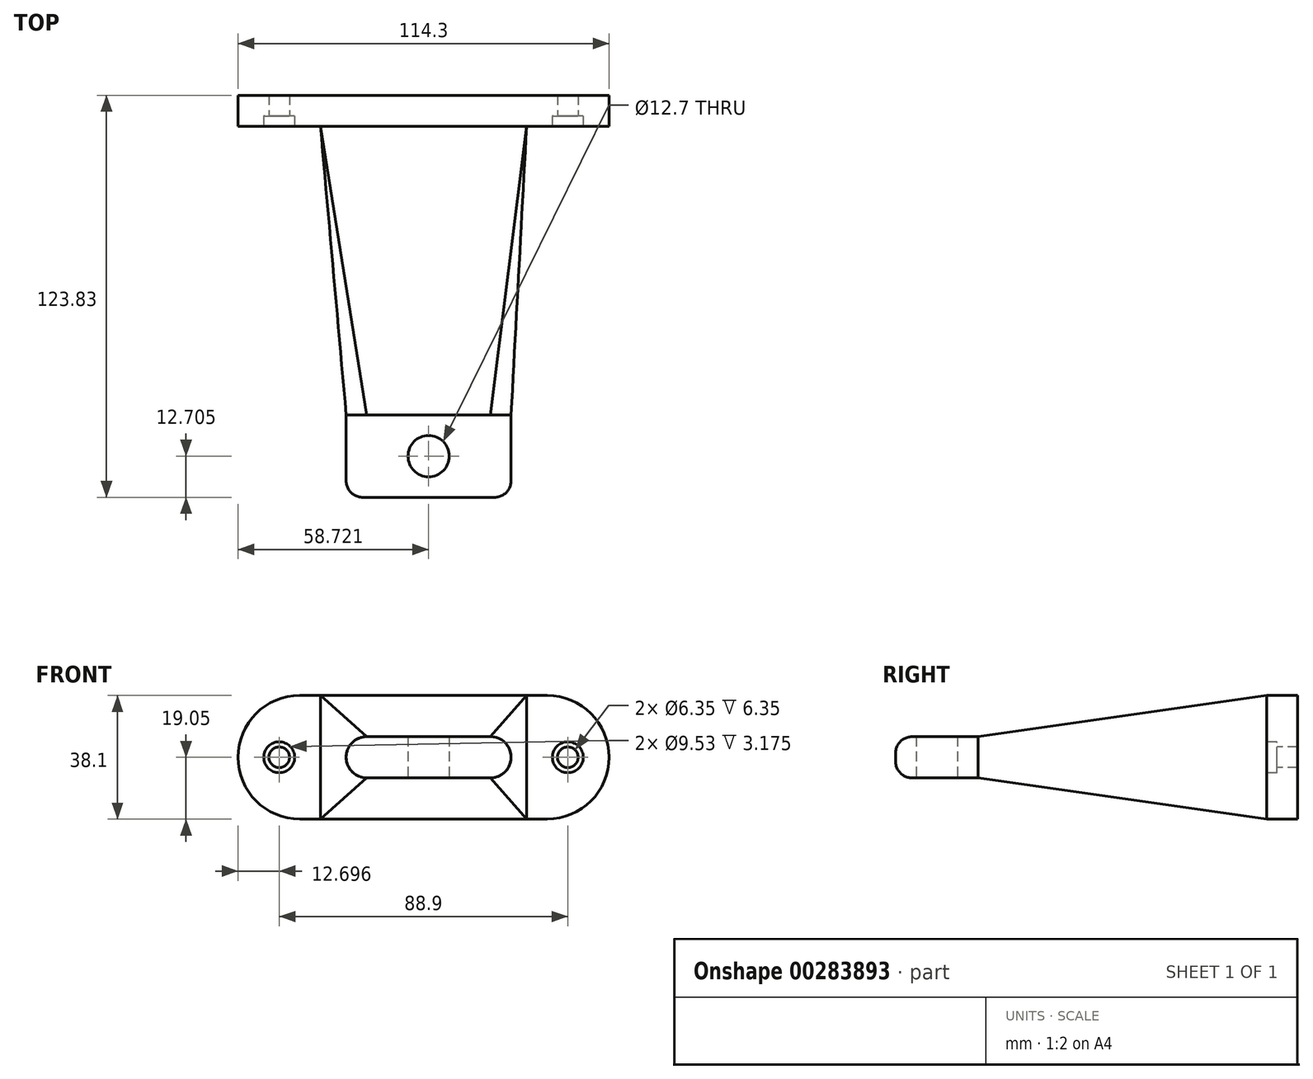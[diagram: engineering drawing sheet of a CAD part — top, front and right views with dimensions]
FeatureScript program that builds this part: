
annotation { "Feature Type Name" : "Feature", "Feature Type Description" : "" }
export const myFeature = defineFeature(function(context is Context, id is Id, definition is map)
    precondition{}
    {
        {
            var Q0;
            Q0=qCreatedBy(makeId("Front.planeOp"),FACE);
            var sketch = newSketch(context, id + "F0", { "sketchPlane" : qUnion([Q0])});
            skArc(sketch, "E0", {"start": v(-42.12, 19.05) * mm, "mid": v(-61.17, 0) * mm, "end": v(-42.12, -19.05) * mm});
            skArc(sketch, "E1", {"start": v(34.08, -19.05) * mm, "mid": v(53.13, 0) * mm, "end": v(34.08, 19.05) * mm});
            skLineSegment(sketch, "E2", {"start": v(-42.12, 19.05) * mm, "end": v(34.08, 19.05) * mm});
            skLineSegment(sketch, "E3", {"start": v(-42.12, -19.05) * mm, "end": v(34.08, -19.05) * mm});
            skSolve(sketch);
        }
        {
            var Q0;
            Q0 = qSketchRegion(id + "F0", true);
            extrude(context, id + "F1", {"entities" : qUnion([Q0]), "depth" : 9.52 * mm});
        }
        {
            var Q0;
            Q0=makeQuery(id+"F1.opExtrude","CAP_FACE",FACE,{"disambiguationData":[OSD([sQuery(id+"F0.wireOp",EDGE,"E0"),sQuery(id+"F0.wireOp",EDGE,"E1"),sQuery(id+"F0.wireOp",EDGE,"E2"),sQuery(id+"F0.wireOp",EDGE,"E3")])],"isStart":false});
            var sketch = newSketch(context, id + "F2", { "sketchPlane" : qUnion([Q0])});
            skLineSegment(sketch, "E4.0.0", {"start": v(-42.12, -19.05) * mm, "end": v(34.08, -19.05) * mm});
            skArc(sketch, "E4.0.1", {"start": v(34.08, -19.05) * mm, "mid": v(53.13, 0) * mm, "end": v(34.08, 19.05) * mm});
            skLineSegment(sketch, "E4.0.2", {"start": v(34.08, 19.05) * mm, "end": v(-42.12, 19.05) * mm});
            skArc(sketch, "E4.0.3", {"start": v(-42.12, 19.05) * mm, "mid": v(-61.17, 0) * mm, "end": v(-42.12, -19.05) * mm});
            skPoint(sketch, "E5", {"position": v(-48.47, 0) * mm});
            skPoint(sketch, "E6", {"position": v(40.43, 0) * mm});
            skSolve(sketch);
        }
        {
            var Q0;
            Q0=sQuery(id+"F2.wireOp",VERTEX,"E5");
            var Q1;
            Q1=sQuery(id+"F2.wireOp",VERTEX,"E6");
            var Q2;
            Q2=makeQuery(id+"F1.opExtrude","SWEPT_BODY",BODY,{"disambiguationData":[OSD([sQuery(id+"F0.wireOp",EDGE,"E0"),sQuery(id+"F0.wireOp",EDGE,"E1"),sQuery(id+"F0.wireOp",EDGE,"E2"),sQuery(id+"F0.wireOp",EDGE,"E3")])]});
            hole(context, id + "F3", {"style" : HoleStyle.C_BORE, "endStyle" : HoleEndStyle.THROUGH, "holeDiameter" : 6.35 * mm, "cBoreDiameter" : 9.52 * mm, "cBoreDepth" : 3.17 * mm, "tappedDepth" : 12.7 * mm, "tapClearance" : 3, "locations" : qUnion([Q0, Q1]), "scope" : qUnion([Q2])});
        }
        {
            var Q0;
            Q0=makeQuery(id+"F1.opExtrude","CAP_FACE",FACE,{"disambiguationData":[OSD([sQuery(id+"F0.wireOp",EDGE,"E0"),sQuery(id+"F0.wireOp",EDGE,"E1"),sQuery(id+"F0.wireOp",EDGE,"E2"),sQuery(id+"F0.wireOp",EDGE,"E3")])],"isStart":false});
            var sketch = newSketch(context, id + "F4", { "sketchPlane" : qUnion([Q0])});
            skLineSegment(sketch, "E7.left", {"start": v(-35.77, 19.05) * mm, "end": v(-35.77, -19.05) * mm});
            skLineSegment(sketch, "E7.right", {"start": v(27.73, 19.05) * mm, "end": v(27.73, -19.05) * mm});
            skLineSegment(sketch, "E8.0.0", {"start": v(-42.12, -19.05) * mm, "end": v(34.08, -19.05) * mm});
            skArc(sketch, "E8.0.1", {"start": v(34.08, -19.05) * mm, "mid": v(53.13, 0) * mm, "end": v(34.08, 19.05) * mm});
            skLineSegment(sketch, "E8.0.2", {"start": v(34.08, 19.05) * mm, "end": v(-42.12, 19.05) * mm});
            skArc(sketch, "E8.0.3", {"start": v(-42.12, 19.05) * mm, "mid": v(-61.17, 0) * mm, "end": v(-42.12, -19.05) * mm});
            skSolve(sketch);
        }
        {
            var Q0;
            {var subQ0=sQuery(id+"F4.wireOp",EDGE,"E7.left");Q0=makeQuery(id+"F4.imprint","IMPRINT",FACE,{"disambiguationData":[TD([[makeQuery(id+"F4.imprint","IMPRINT",EDGE,{"derivedFrom":subQ0}),1.0]])]});}
            cPlane(context, id + "F5", {"entities" : qUnion([Q0]), "cplaneType" : CPlaneType.OFFSET, "offset" : 88.9 * mm, "width" : 152.4 * mm, "height" : 152.4 * mm});
        }
        {
            var Q0;
            Q0=qCreatedBy(id+"F5.planeOp",FACE);
            var sketch = newSketch(context, id + "F6", { "sketchPlane" : qUnion([Q0])});
            skArc(sketch, "E9", {"start": v(-21.5, 6.35) * mm, "mid": v(-27.85, 0) * mm, "end": v(-21.5, -6.35) * mm});
            skArc(sketch, "E10", {"start": v(16.6, -6.35) * mm, "mid": v(22.95, 0) * mm, "end": v(16.6, 6.35) * mm});
            skLineSegment(sketch, "E11", {"start": v(-21.5, 6.35) * mm, "end": v(16.6, 6.35) * mm});
            skLineSegment(sketch, "E12", {"start": v(-21.5, -6.35) * mm, "end": v(16.6, -6.35) * mm});
            skSolve(sketch);
        }
        {
            var Q1;
            Q1=makeQuery(id+"F6.imprint","IMPRINT",FACE,{"disambiguationData":[TD([[makeQuery(id+"F6.imprint","IMPRINT",EDGE,{"derivedFrom":sQuery(id+"F6.wireOp",EDGE,"E9")}),1.0]])]});
            var Q2;
            {var subQ0=sQuery(id+"F4.wireOp",EDGE,"E7.left");Q2=makeQuery(id+"F4.imprint","IMPRINT",FACE,{"disambiguationData":[TD([[makeQuery(id+"F4.imprint","IMPRINT",EDGE,{"derivedFrom":subQ0}),1.0]])]});}
            loft(context, id + "F7", {"operationType" : NewBodyOperationType.ADD, "sheetProfilesArray" : [{ "sheetProfileEntities" : qUnion([Q1]) }, { "sheetProfileEntities" : qUnion([Q2]) }]});
        }
        {
            var Q0;
            Q0=makeQuery(id+"F7.opLoft","CAP_FACE",FACE,{"disambiguationData":[OSD([makeQuery(id+"F6.imprint","IMPRINT",FACE,{"disambiguationData":[TD([[makeQuery(id+"F6.imprint","IMPRINT",EDGE,{"derivedFrom":sQuery(id+"F6.wireOp",EDGE,"E9")}),1.0]])]})])],"isStart":true});
            extrude(context, id + "F8", {"entities" : qUnion([Q0]), "operationType" : NewBodyOperationType.ADD, "depth" : 25.4 * mm});
        }
        {
            var Q0;
            Q0=makeQuery(id+"F8.opExtrude","SWEPT_FACE",FACE,{"disambiguationData":[OSD([sQuery(id+"F6.wireOp",EDGE,"E9"),sQuery(id+"F6.wireOp",EDGE,"E10"),sQuery(id+"F6.wireOp",EDGE,"E12")])]});
            var sketch = newSketch(context, id + "F9", { "sketchPlane" : qUnion([Q0])});
            skPoint(sketch, "E13", {"position": v(-2.45, 111.13) * mm});
            skPoint(sketch, "E13.positionSnap0", {"position": v(-2.45, 123.83) * mm});
            skSolve(sketch);
        }
        {
            var Q0;
            Q0=sQuery(id+"F9.wireOp",VERTEX,"E13");
            var Q1;
            Q1=makeQuery(id+"F1.opExtrude","SWEPT_BODY",BODY,{"disambiguationData":[OSD([sQuery(id+"F0.wireOp",EDGE,"E0"),sQuery(id+"F0.wireOp",EDGE,"E1"),sQuery(id+"F0.wireOp",EDGE,"E2"),sQuery(id+"F0.wireOp",EDGE,"E3")])]});
            hole(context, id + "F10", {"style" : HoleStyle.SIMPLE, "endStyle" : HoleEndStyle.THROUGH, "holeDiameter" : 12.7 * mm, "tappedDepth" : 12.7 * mm, "tapClearance" : 3, "locations" : qUnion([Q0]), "scope" : qUnion([Q1])});
        }
        {
            var Q0;
            Q0=makeQuery(id+"F8.opExtrude","CAP_EDGE",EDGE,{"disambiguationData":[OSD([sQuery(id+"F6.wireOp",EDGE,"E9"),sQuery(id+"F6.wireOp",EDGE,"E10"),sQuery(id+"F6.wireOp",EDGE,"E12")])],"isStart":false});
            var Q1;
            Q1=makeQuery(id+"F8.opExtrude","CAP_EDGE",EDGE,{"disambiguationData":[OSD([sQuery(id+"F6.wireOp",EDGE,"E10"),sQuery(id+"F6.wireOp",EDGE,"E11"),sQuery(id+"F6.wireOp",EDGE,"E12")])],"isStart":false});
            fillet(context, id + "F11", {"entities" : qUnion([Q0, Q1]), "radius" : 5.08 * mm, "tangentPropagation" : true, "allowEdgeOverflow" : false});
        }
    });
